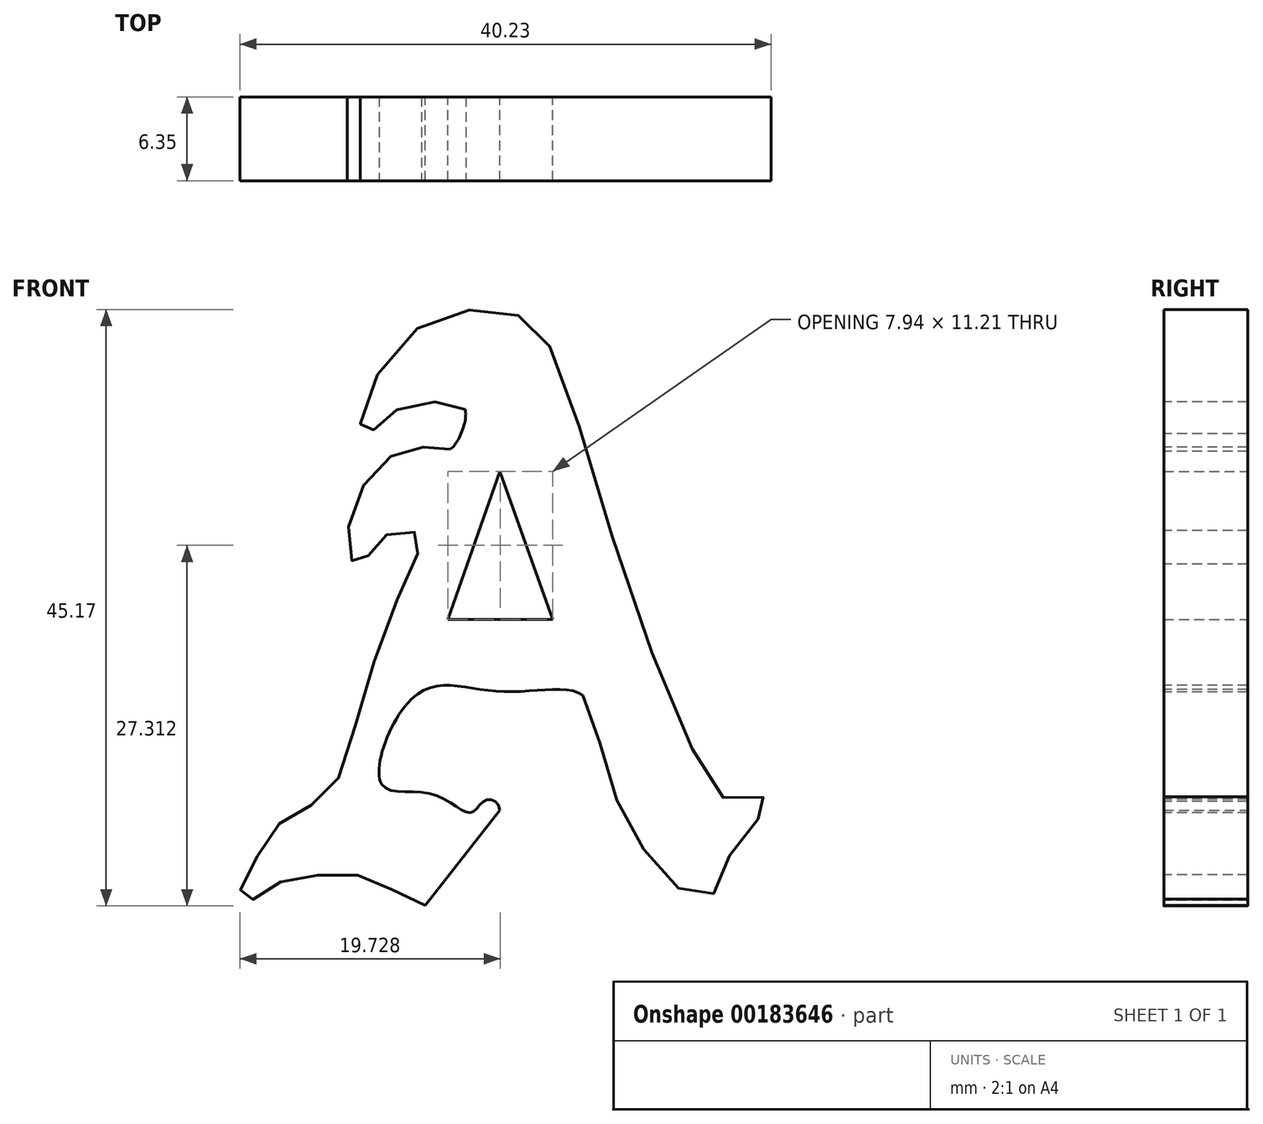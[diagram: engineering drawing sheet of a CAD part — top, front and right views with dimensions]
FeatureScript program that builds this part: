
annotation { "Feature Type Name" : "Feature", "Feature Type Description" : "" }
export const myFeature = defineFeature(function(context is Context, id is Id, definition is map)
    precondition{}
    {
        {
            var Q0;
            Q0=qCreatedBy(makeId("Front.planeOp"),FACE);
            var sketch = newSketch(context, id + "F0", { "sketchPlane" : qUnion([Q0])});
            skFitSpline(sketch, "E0", {"points": [v(-5.65, -14.34) * mm, v(-8.88, -12.6) * mm, v(-12.65, -12.06) * mm, v(-16.5, -12.53) * mm, v(-18.87, -13.94) * mm, v(-19.65, -13.63) * mm, v(-18.55, -10.96) * mm, v(-16.2, -7.73) * mm, v(-13.05, -5.92) * mm, v(-10.45, 1.08) * mm, v(-6.76, 11.14) * mm, v(-6.05, 13.66) * mm, v(-7.86, 13.97) * mm, v(-9.43, 12.95) * mm, v(-10.53, 11.53) * mm, v(-11.32, 11.93) * mm, v(-11.08, 15.86) * mm, v(-8.49, 19.48) * mm, v(-5.65, 20.34) * mm, v(-3.77, 20.18) * mm, v(-2.62, 23.2) * mm, v(-3.8, 23.73) * mm, v(-6.74, 23.61) * mm, v(-8.63, 22.58) * mm, v(-9.67, 21.57) * mm, v(-10.26, 21.39) * mm, v(-10.56, 22.17) * mm, v(-8.4, 27.18) * mm, v(-3.73, 30.52) * mm, v(1.02, 30.44) * mm, v(3.47, 28.55) * mm, v(9.02, 12.04) * mm, v(16.03, -5.17) * mm, v(18.09, -6.48) * mm, v(20.52, -6.2) * mm, v(18.83, -8.63) * mm, v(17.06, -11.34) * mm, v(15.84, -13.77) * mm, v(13.04, -12.65) * mm, v(10.04, -8.63) * mm, v(7.8, -3.2) * mm, v(6.3, 1.56) * mm, v(0, 1.84) * mm, v(-6.23, 1.66) * mm, v(-8.94, -5.17) * mm, v(-5.1, -5.92) * mm, v(-2.2, -7.32) * mm, v(-1.08, -6.38) * mm, v(0, -7.13) * mm, v(-5.65, -14.34) * mm]});
            skLineSegment(sketch, "E1", {"start": v(6.3, 1.56) * mm, "end": v(-6.23, 1.66) * mm});
            skLineSegment(sketch, "E2", {"start": v(-6.23, 1.66) * mm, "end": v(-8.94, -5.17) * mm});
            skLineSegment(sketch, "E3", {"start": v(0, -7.13) * mm, "end": v(-5.65, -14.34) * mm});
            skLineSegment(sketch, "E4", {"start": v(0, 18.53) * mm, "end": v(-3.92, 7.32) * mm});
            skLineSegment(sketch, "E5", {"start": v(-3.92, 7.32) * mm, "end": v(4.02, 7.32) * mm});
            skLineSegment(sketch, "E6", {"start": v(4.02, 7.32) * mm, "end": v(0, 18.53) * mm});
            skLineSegment(sketch, "E7", {"start": v(-3.77, 20.18) * mm, "end": v(-2.62, 23.2) * mm});
            skSolve(sketch);
        }
        {
            var Q0;
            Q0=makeQuery(id+"F0.imprint","IMPRINT",FACE,{"disambiguationData":[TD([[makeQuery(id+"F0.imprint","IMPRINT",EDGE,{"derivedFrom":sQuery(id+"F0.wireOp",EDGE,"E0")}),-1.0]])]});
            extrude(context, id + "F2", {"entities" : qUnion([Q0]), "depth" : 6.35 * mm});
        }
    });
